# Revit family: Sanitary_Sanitary-Accessories_hansgrohe_27904XXX-WallStoris-Wall-bar-70-cm_NEW
name_source: partatom
category: Furniture
revit_build: Autodesk Revit 2018 (Build: 20170223_1515(x64)
units: mm (PartAtom-declared; Revit-internal decimal feet)

## family parameters
Always vertical = No
Cut with Voids When Loaded = No
OmniClass Number = 23.40.20.00
OmniClass Title = General Furniture and Specialties
Room Calculation Point = No
Shared = No
Work Plane-Based = Yes

## types (2) — shared parameters
Always visible = Yes
BIMobject category = Sanitary Accessories
Default Elevation = 1219.2 mm  [stored 4 ft]
Design country = Germany
EAN code = 4059625352885
Edition number = 1
GTIN code = https://4059625352885
IFC Classification = Sanitary Terminal
Installation instructions = https://www.hansgrohe.com
Manufacturer country = Germany
Manufacturer name = hansgrohe
Product Guid = 9d450c2d-5367-4039-be59-d5f9fa0e6dc2
Product SKU = 27904XXX
Product data url = https://www.bimobject.com
Product family = WallStoris
Product group = Shelfs
Product name = 27904XXX WallStoris Wall bar 70 cm
Product url = https://www.hansgrohe.com
QR code = https://www.bimobject.com
Technical description = https://www.hansgrohe.com

## per-type parameters (varying)
| type | Material 1 |
| 700 Matt White | Hansgrohe - WallStoris - 700 Matt White |
| 670 Matte Black | Hansgrohe - WallStoris - 670 Matte Black |

note: [stored X ft] marks values corroborated as IEEE doubles in the binary element streams (Revit-internal decimal feet)

## geometry (parser evidence)
native form markers: Sweep x3
no freeform markers — native parametric forms only
